# Revit family: Storage-Teknion-C1HS_Single_Credenza-R2021
name_source: partatom
category: Furniture
units: mm (PartAtom-declared; Revit-internal decimal feet)

## family parameters
Always vertical = Yes
Cut with Voids When Loaded = No
OmniClass Number = 23.40.20.00
OmniClass Title = General Furniture and Specialties
Room Calculation Point = No
Shared = Yes
Work Plane-Based = No

## types (6) — shared parameters
Assembly Code = E2020200
Manufacturer = Teknion
Manufacturer Fax = 416.661.4586
Part Number = C1HS
Series = Chronicle
Sustainability Data = https://www.teknion.com
URL = www.teknion.com
Unit Weight URL = http://www.teknion.com
Warranty = http://www.teknion.com
zero-valued in all types: Default Elevation

## per-type parameters (varying)
| type | 2 File (F) | 2D - Door 1 | 2D - Door 2 | 2D - Drawer | Case - Back (Open) | Case - Top | Cut-Out - Front - 1 | Cut-Out - Front - 2 | Cut-Out - Front - 3 | Description | Dim - Case 1 | Dim 1 - Case - Back | Dim 2 - Case - Back | Distance - Shelf Panel | Drawer 1 | Drawer 2 | Drawer 3 | Drawer 4 | Front | Model | Open (O) | Shelf - Hinged Doors & Open |
| Waste Bin Drawer | No | Yes | No | Yes | No | Yes | 0.5 " | 5 " | 0.5 " | Single Credenza, Waste Bin Drawer Storage Configuration | 0.843 " | 1.5 " | 1.539 " | 1.843 " | No | No | No | Yes | Yes | C1HSW___ | No | No |
| Open | No | No | No | No | Yes | No | 0.5 " | 0.5 " | 0.5 " | Single Credenza, Open Storage Configuration | 0 " | 5.5 " | 1.854 " | 1 " | No | No | No | No | No | C1HSO___ | Yes | Yes |
| Hinged Doors With Printer Shelf | No | No | Yes | No | No | Yes | 0.5 " | 0.5 " | 6 " | Single Credenza, Hinged Doors With Printer Shelf Storage Configuration | 0.843 " | 1.5 " | 1.539 " | 1.843 " | No | No | No | No | Yes | C1HSP___ | No | No |
| Hinged Doors | No | No | Yes | No | No | Yes | 0.5 " | 0.5 " | 6 " | Single Credenza, Hinged Doors Storage Configuration | 0.843 " | 1.5 " | 1.539 " | 1.843 " | No | No | No | No | Yes | C1HSH___ | No | Yes |
| 2 File | Yes | Yes | No | Yes | No | Yes | 5 " | 0.5 " | 0.5 " | Single Credenza, 2 File Storage Configuration | 0.843 " | 1.5 " | 1.539 " | 1.843 " | Yes | Yes | No | No | Yes | C1HSF___ | No | No |
| 2 Box 1 File | No | Yes | No | Yes | No | Yes | 5 " | 5 " | 0.5 " | Single Credenza, 2 Box 1 File Storage Configuration | 0.843 " | 1.5 " | 1.539 " | 1.843 " | Yes | No | Yes | Yes | Yes | C1HSB___ | No | No |

type visibility flags (boolean, named after types; folded from table):
- Waste Bin Drawer: Yes: Waste Bin Drawer (W)
- Open: Yes: (none)
- Hinged Doors With Printer Shelf: Yes: Hinged Doors With Printer Shelf (P)
- Hinged Doors: Yes: Hinged Doors (H)
- 2 File: Yes: (none)
- 2 Box 1 File: Yes: 2 Box 1 File (B)

## geometry (parser evidence)
native form markers: Sweep x2
no freeform markers — native parametric forms only
